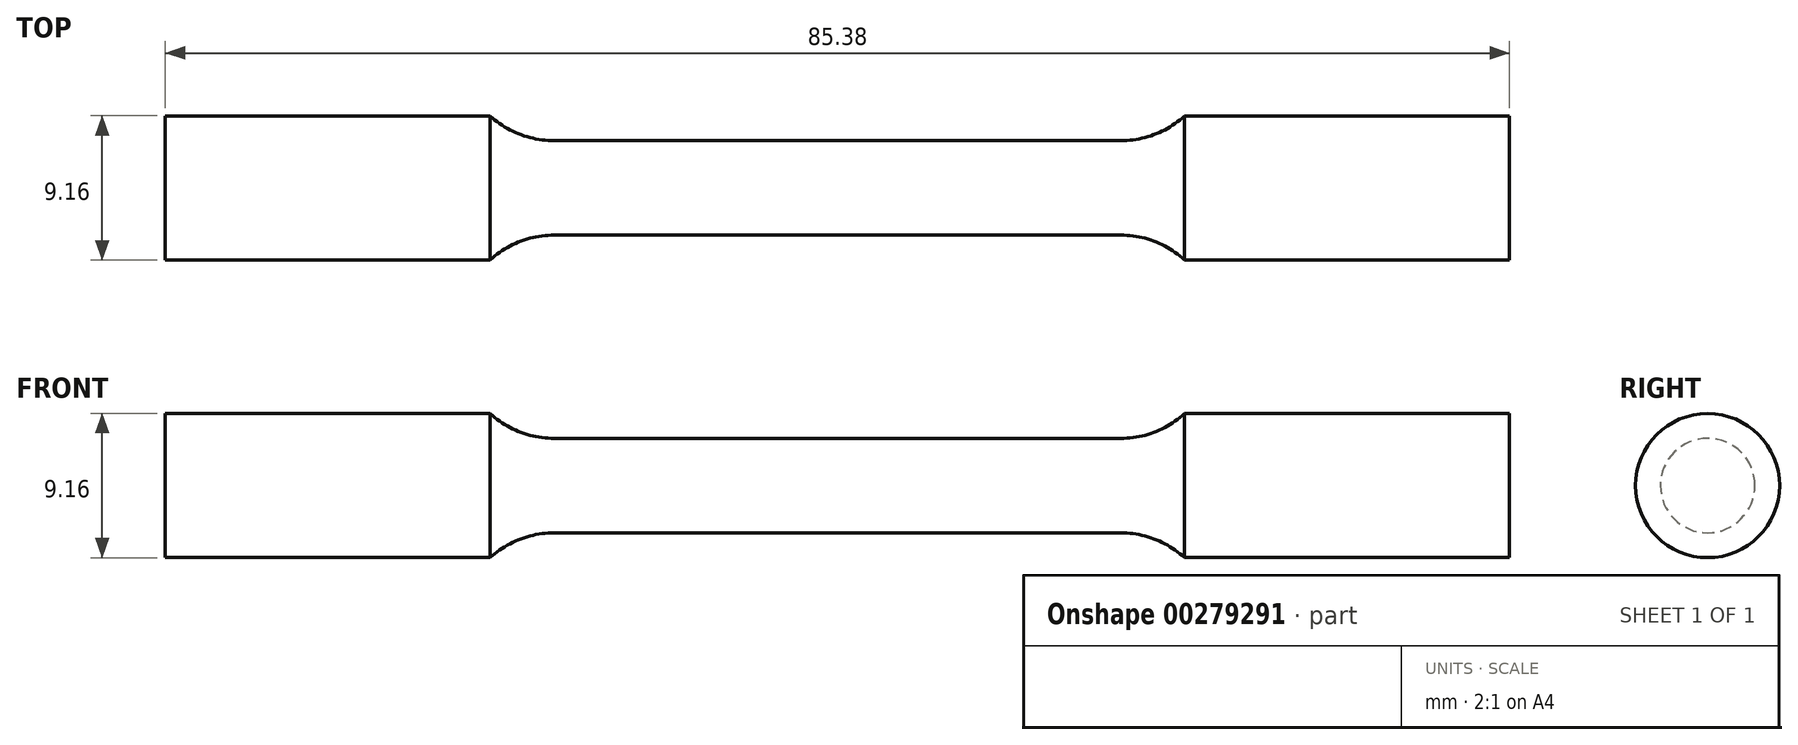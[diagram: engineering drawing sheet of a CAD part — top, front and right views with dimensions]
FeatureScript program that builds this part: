
annotation { "Feature Type Name" : "Feature", "Feature Type Description" : "" }
export const myFeature = defineFeature(function(context is Context, id is Id, definition is map)
    precondition{}
    {
        {
            var Q0;
            Q0=qCreatedBy(makeId("Front.planeOp"),FACE);
            var sketch = newSketch(context, id + "F0", { "sketchPlane" : qUnion([Q0])});
            skLineSegment(sketch, "E0", {"start": v(0, 3) * mm, "end": v(18, 3) * mm});
            skArc(sketch, "E1", {"start": v(18, 3) * mm, "mid": v(20.17, 3.4) * mm, "end": v(22.05, 4.58) * mm});
            skLineSegment(sketch, "E2", {"start": v(22.05, 4.58) * mm, "end": v(42.69, 4.58) * mm});
            skLineSegment(sketch, "E3", {"start": v(42.69, 4.58) * mm, "end": v(42.69, 0) * mm});
            skLineSegment(sketch, "E4.MirrorCS", {"start": v(0, 3) * mm, "end": v(-18, 3) * mm});
            skLineSegment(sketch, "E5.MirrorCS", {"start": v(-42.69, 4.58) * mm, "end": v(-42.69, 0) * mm});
            skLineSegment(sketch, "E6.MirrorCS", {"start": v(-22.05, 4.58) * mm, "end": v(-42.69, 4.58) * mm});
            skArc(sketch, "E7.MirrorCS", {"start": v(-18, 3) * mm, "mid": v(-20.17, 3.4) * mm, "end": v(-22.05, 4.58) * mm});
            skLineSegment(sketch, "E8", {"start": v(-42.69, 0) * mm, "end": v(42.69, 0) * mm});
            skSolve(sketch);
        }
        {
            var Q0;
            Q0 = qSketchRegion(id + "F0", true);
            var Q1;
            Q1=sQuery(id+"F0.wireOp",EDGE,"E8");
            revolve(context, id + "F1", {"entities" : qUnion([Q0]), "axis" : qUnion([Q1]), "revolveType" : RevolveType.FULL});
        }
    });
